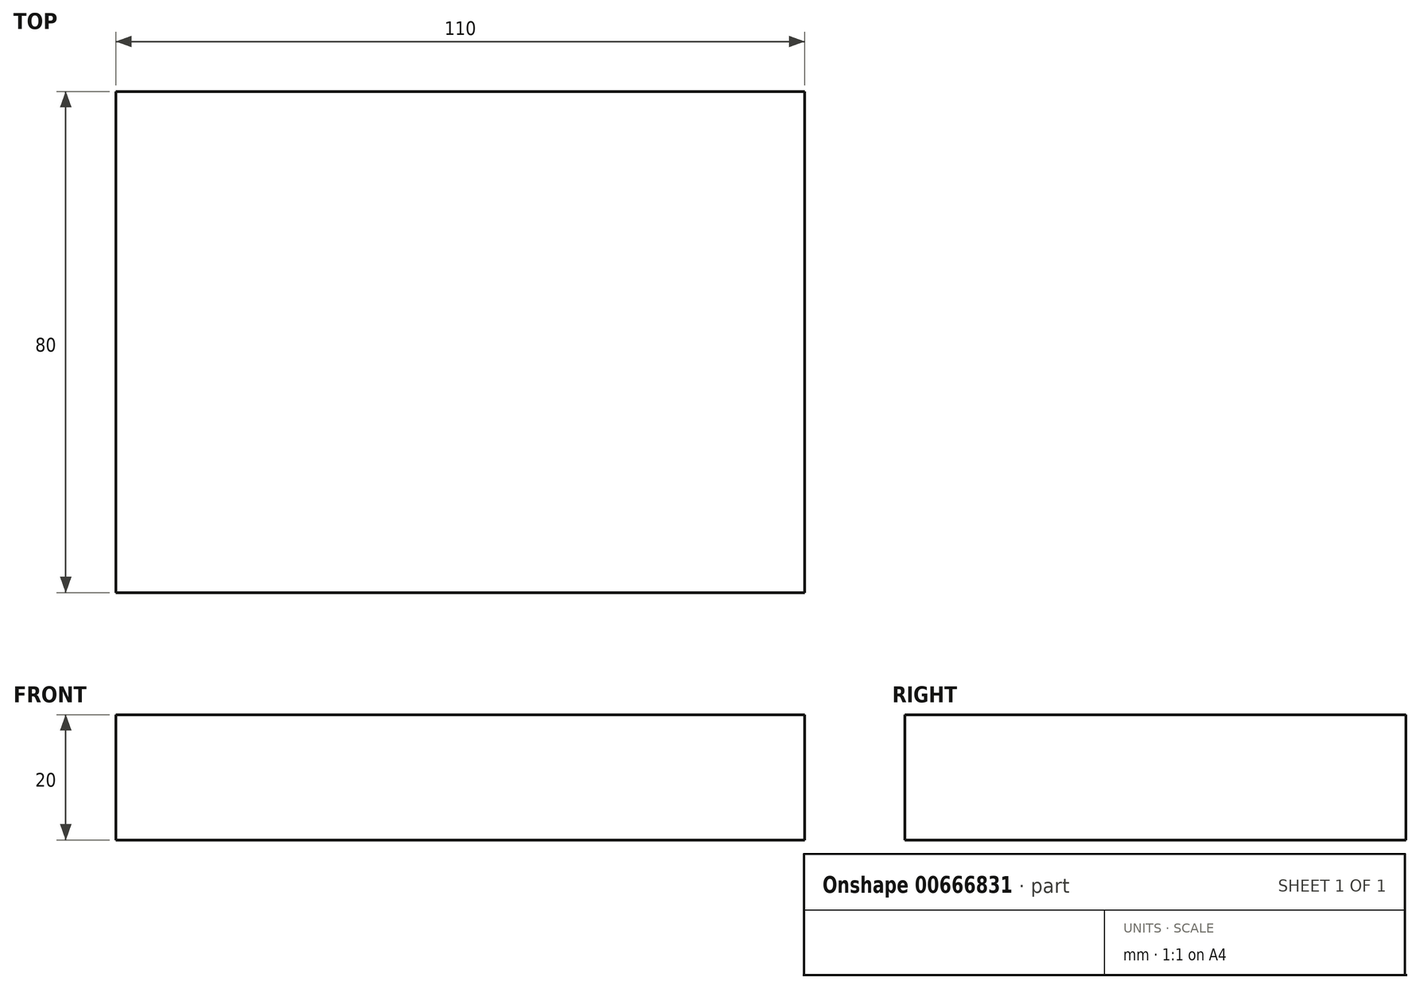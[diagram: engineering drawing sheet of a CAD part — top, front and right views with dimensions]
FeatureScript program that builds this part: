
annotation { "Feature Type Name" : "Feature", "Feature Type Description" : "" }
export const myFeature = defineFeature(function(context is Context, id is Id, definition is map)
    precondition{}
    {
        {
            var Q0;
            Q0=qCreatedBy(makeId("Top.planeOp"),FACE);
            var sketch = newSketch(context, id + "F0", { "sketchPlane" : qUnion([Q0])});
            skLineSegment(sketch, "E0.bottom", {"start": v(0, 0) * mm, "end": v(110, 0) * mm});
            skLineSegment(sketch, "E0.top", {"start": v(0, 80) * mm, "end": v(110, 80) * mm});
            skLineSegment(sketch, "E0.left", {"start": v(0, 0) * mm, "end": v(0, 80) * mm});
            skLineSegment(sketch, "E0.right", {"start": v(110, 0) * mm, "end": v(110, 80) * mm});
            skSolve(sketch);
        }
        {
            var Q0;
            Q0 = qSketchRegion(id + "F0", true);
            extrude(context, id + "F1", {"entities" : qUnion([Q0]), "depth" : 20 * mm, "offsetDistance" : 25 * mm});
        }
    });
